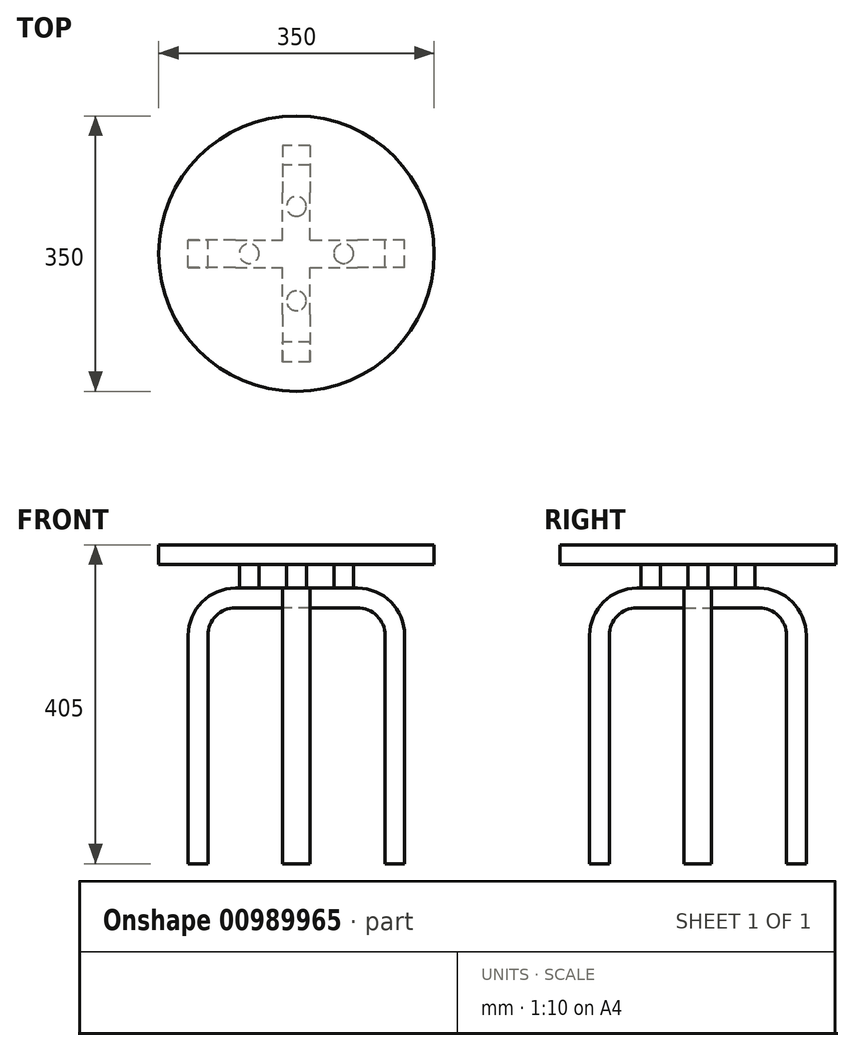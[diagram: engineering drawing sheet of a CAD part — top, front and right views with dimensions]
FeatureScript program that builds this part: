
annotation { "Feature Type Name" : "Feature", "Feature Type Description" : "" }
export const myFeature = defineFeature(function(context is Context, id is Id, definition is map)
    precondition{}
    {
        {
            var Q0;
            Q0=qCreatedBy(makeId("Front.planeOp"),FACE);
            var sketch = newSketch(context, id + "F0", { "sketchPlane" : qUnion([Q0])});
            skLineSegment(sketch, "E0", {"start": v(-137.5, 0) * mm, "end": v(-112.5, 0) * mm});
            skLineSegment(sketch, "E1", {"start": v(-112.5, 0) * mm, "end": v(-112.5, 290) * mm});
            skLineSegment(sketch, "E2", {"start": v(-77.5, 325) * mm, "end": v(0, 325) * mm});
            skLineSegment(sketch, "E3", {"start": v(0, 325) * mm, "end": v(0, 350) * mm, "construction": true});
            skLineSegment(sketch, "E4", {"start": v(0, 350) * mm, "end": v(-77.5, 350) * mm});
            skLineSegment(sketch, "E5", {"start": v(-137.5, 290) * mm, "end": v(-137.5, 0) * mm});
            skPoint(sketch, "E6.visualSharp", {"position": v(-137.5, 350) * mm});
            skArc(sketch, "E6.filletArc", {"start": v(-77.5, 350) * mm, "mid": v(-119.93, 332.43) * mm, "end": v(-137.5, 290) * mm});
            skArc(sketch, "E7.0", {"start": v(-77.5, 325) * mm, "mid": v(-102.25, 314.75) * mm, "end": v(-112.5, 290) * mm});
            skLineSegment(sketch, "E8.MirrorCS", {"start": v(0, 350) * mm, "end": v(77.5, 350) * mm});
            skLineSegment(sketch, "E9.MirrorCS", {"start": v(77.5, 325) * mm, "end": v(0, 325) * mm});
            skArc(sketch, "E10.MirrorCS", {"start": v(77.5, 325) * mm, "mid": v(102.25, 314.75) * mm, "end": v(112.5, 290) * mm});
            skArc(sketch, "E11.MirrorCS", {"start": v(77.5, 350) * mm, "mid": v(119.93, 332.43) * mm, "end": v(137.5, 290) * mm});
            skLineSegment(sketch, "E12.MirrorCS", {"start": v(137.5, 290) * mm, "end": v(137.5, 0) * mm});
            skLineSegment(sketch, "E13.MirrorCS", {"start": v(112.5, 0) * mm, "end": v(112.5, 290) * mm});
            skLineSegment(sketch, "E14.MirrorCS", {"start": v(137.5, 0) * mm, "end": v(112.5, 0) * mm});
            skSolve(sketch);
        }
        {
            var Q0;
            Q0=makeQuery(id+"F0.imprint","IMPRINT",FACE,{"disambiguationData":[TD([[makeQuery(id+"F0.imprint","IMPRINT",EDGE,{"derivedFrom":sQuery(id+"F0.wireOp",EDGE,"E0")}),1.0]])]});
            extrude(context, id + "F1", {"entities" : qUnion([Q0]), "endBound" : BoundingType.SYMMETRIC, "depth" : 35 * mm, "offsetDistance" : 25 * mm});
        }
        {
            var Q0;
            Q0=makeQuery(id+"F1.opExtrude","SWEPT_BODY",BODY,{"disambiguationData":[OSD([sQuery(id+"F0.wireOp",EDGE,"E0"),sQuery(id+"F0.wireOp",EDGE,"E1"),sQuery(id+"F0.wireOp",EDGE,"E2"),sQuery(id+"F0.wireOp",EDGE,"E4"),sQuery(id+"F0.wireOp",EDGE,"E5"),sQuery(id+"F0.wireOp",EDGE,"E6.filletArc"),sQuery(id+"F0.wireOp",EDGE,"E7.0"),sQuery(id+"F0.wireOp",EDGE,"E8.MirrorCS"),sQuery(id+"F0.wireOp",EDGE,"E9.MirrorCS"),sQuery(id+"F0.wireOp",EDGE,"E10.MirrorCS"),sQuery(id+"F0.wireOp",EDGE,"E11.MirrorCS"),sQuery(id+"F0.wireOp",EDGE,"E12.MirrorCS"),sQuery(id+"F0.wireOp",EDGE,"E13.MirrorCS"),sQuery(id+"F0.wireOp",EDGE,"E14.MirrorCS")])]});
            var Q1;
            Q1=sQuery(id+"F0.wireOp",EDGE,"E3");
            circularPattern(context, id + "F2", {"operationType" : NewBodyOperationType.ADD, "entities" : qUnion([Q0]), "axis" : qUnion([Q1]), "angle" : 90 * degree, "instanceCount" : 2, "equalSpace" : true});
        }
        {
            var Q0;
            Q0=qCreatedBy(makeId("Top.planeOp"),FACE);
            cPlane(context, id + "F3", {"entities" : qUnion([Q0]), "cplaneType" : CPlaneType.OFFSET, "offset" : 380 * mm, "width" : 150 * mm, "height" : 150 * mm});
        }
        {
            var Q0;
            Q0=qCreatedBy(id+"F3.planeOp",FACE);
            var sketch = newSketch(context, id + "F4", { "sketchPlane" : qUnion([Q0])});
            skCircle(sketch, "E15", {"center": v(0, 0) * mm, "radius": 175 * mm});
            skSolve(sketch);
        }
        {
            var Q0;
            Q0=makeQuery(id+"F4.imprint","IMPRINT",FACE,{"disambiguationData":[TD([[makeQuery(id+"F4.imprint","IMPRINT",EDGE,{"derivedFrom":sQuery(id+"F4.wireOp",EDGE,"E15")}),1.0]])]});
            extrude(context, id + "F5", {"entities" : qUnion([Q0]), "depth" : 25 * mm, "offsetDistance" : 25 * mm});
        }
        {
            var Q0;
            {var subQ0=makeQuery(id+"F1.opExtrude","SWEPT_FACE",FACE,{"disambiguationData":[OSD([sQuery(id+"F0.wireOp",EDGE,"E4"),sQuery(id+"F0.wireOp",EDGE,"E8.MirrorCS")])]});Q0=makeQuery(id+"F2.boolean.opBoolean","MERGE",FACE,{"derivedFrom":[subQ0,makeQuery(id+"F2.opPattern","COPY",FACE,{"derivedFrom":subQ0,"instanceName":"1"})]});}
            var sketch = newSketch(context, id + "F6", { "sketchPlane" : qUnion([Q0])});
            skCircle(sketch, "E16", {"center": v(-60, 0) * mm, "radius": 12.5 * mm});
            skSolve(sketch);
        }
        {
            var Q0;
            Q0 = qSketchRegion(id + "F6", true);
            extrude(context, id + "F7", {"entities" : qUnion([Q0]), "operationType" : NewBodyOperationType.ADD, "endBound" : BoundingType.UP_TO_NEXT, "depth" : 25 * mm, "offsetDistance" : 25 * mm});
        }
        {
            var Q0;
            Q0=makeQuery(id+"F1.opExtrude","SWEPT_BODY",BODY,{"disambiguationData":[OSD([sQuery(id+"F0.wireOp",EDGE,"E0"),sQuery(id+"F0.wireOp",EDGE,"E1"),sQuery(id+"F0.wireOp",EDGE,"E2"),sQuery(id+"F0.wireOp",EDGE,"E4"),sQuery(id+"F0.wireOp",EDGE,"E5"),sQuery(id+"F0.wireOp",EDGE,"E6.filletArc"),sQuery(id+"F0.wireOp",EDGE,"E7.0"),sQuery(id+"F0.wireOp",EDGE,"E8.MirrorCS"),sQuery(id+"F0.wireOp",EDGE,"E9.MirrorCS"),sQuery(id+"F0.wireOp",EDGE,"E10.MirrorCS"),sQuery(id+"F0.wireOp",EDGE,"E11.MirrorCS"),sQuery(id+"F0.wireOp",EDGE,"E12.MirrorCS"),sQuery(id+"F0.wireOp",EDGE,"E13.MirrorCS"),sQuery(id+"F0.wireOp",EDGE,"E14.MirrorCS")])]});
            var Q1;
            Q1=sQuery(id+"F0.wireOp",EDGE,"E3");
            circularPattern(context, id + "F8", {"operationType" : NewBodyOperationType.ADD, "entities" : qUnion([Q0]), "axis" : qUnion([Q1]), "angle" : 360 * degree, "instanceCount" : 4, "equalSpace" : true});
        }
    });
